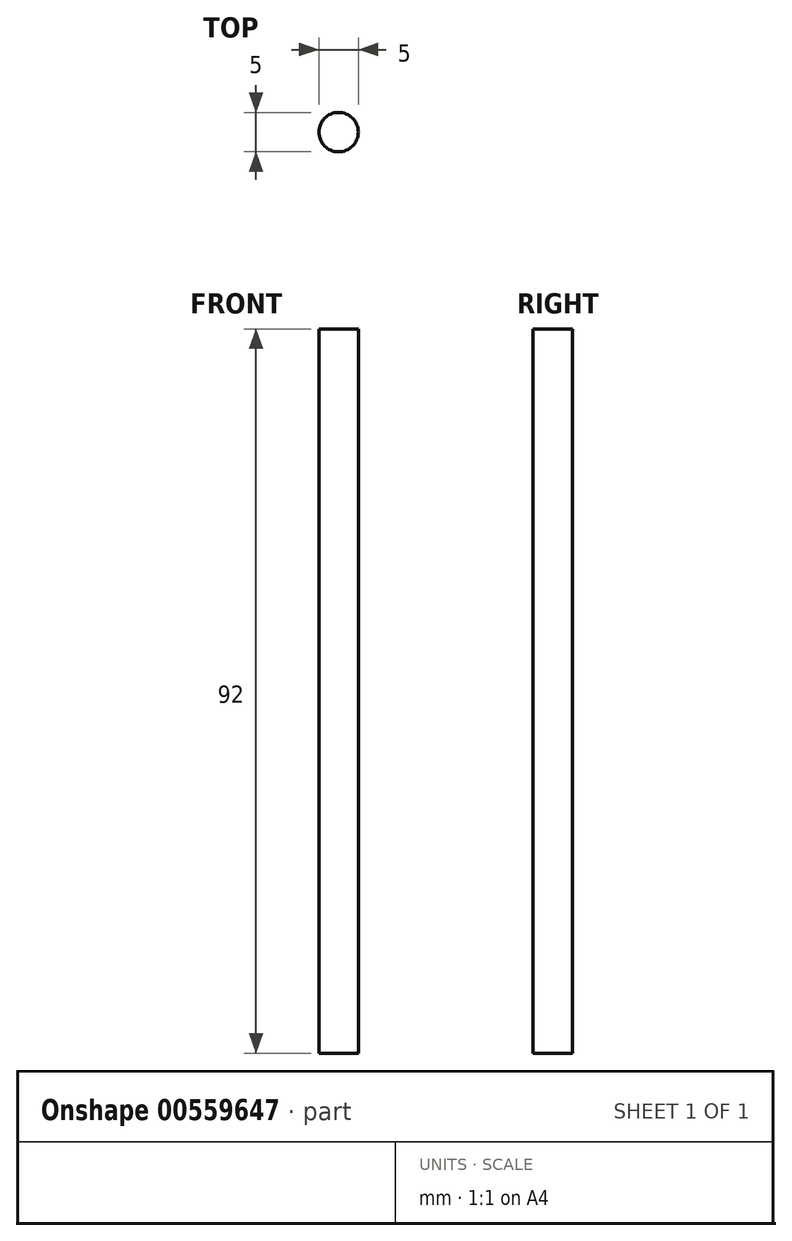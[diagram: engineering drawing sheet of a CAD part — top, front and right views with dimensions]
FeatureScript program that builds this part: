
annotation { "Feature Type Name" : "Feature", "Feature Type Description" : "" }
export const myFeature = defineFeature(function(context is Context, id is Id, definition is map)
    precondition{}
    {
        {
            var Q0;
            Q0=qCreatedBy(makeId("Top.planeOp"),FACE);
            var sketch = newSketch(context, id + "F0", { "sketchPlane" : qUnion([Q0])});
            skCircle(sketch, "E0", {"center": v(0, 0) * mm, "radius": 2.5 * mm});
            skSolve(sketch);
        }
        {
            var Q0;
            Q0 = qSketchRegion(id + "F0", true);
            extrude(context, id + "F1", {"entities" : qUnion([Q0]), "depth" : 92 * mm, "offsetDistance" : 25 * mm});
        }
    });
